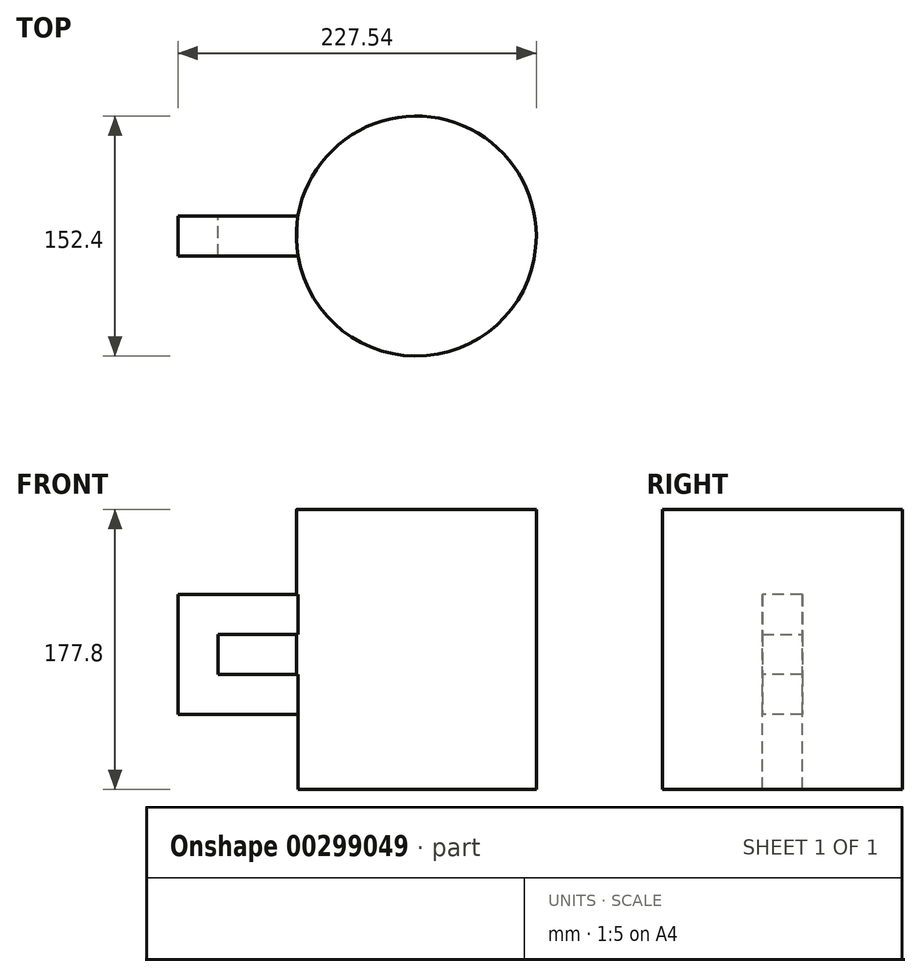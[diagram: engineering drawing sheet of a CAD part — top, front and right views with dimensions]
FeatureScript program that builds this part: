
annotation { "Feature Type Name" : "Feature", "Feature Type Description" : "" }
export const myFeature = defineFeature(function(context is Context, id is Id, definition is map)
    precondition{}
    {
        {
            var Q0;
            Q0=qCreatedBy(makeId("Front.planeOp"),FACE);
            var sketch = newSketch(context, id + "F0", { "sketchPlane" : qUnion([Q0])});
            skLineSegment(sketch, "E0", {"start": v(-88.52, 73.08) * mm, "end": v(-12.32, 73.08) * mm});
            skLineSegment(sketch, "E1", {"start": v(-88.52, 73.08) * mm, "end": v(-88.52, -3.12) * mm});
            skLineSegment(sketch, "E2", {"start": v(-12.32, -3.12) * mm, "end": v(-88.52, -3.12) * mm});
            skLineSegment(sketch, "E3.bottom", {"start": v(-12.32, 47.68) * mm, "end": v(-63.12, 47.68) * mm});
            skLineSegment(sketch, "E3.top", {"start": v(-12.32, 22.28) * mm, "end": v(-63.12, 22.28) * mm});
            skLineSegment(sketch, "E3.right", {"start": v(-63.12, 47.68) * mm, "end": v(-63.12, 22.28) * mm});
            skLineSegment(sketch, "E4", {"start": v(-12.32, 73.08) * mm, "end": v(-12.32, 47.68) * mm});
            skLineSegment(sketch, "E5", {"start": v(-12.32, 22.28) * mm, "end": v(-12.32, -3.12) * mm});
            skSolve(sketch);
        }
        {
            var Q0;
            Q0=makeQuery(id+"F0.imprint","IMPRINT",FACE,{"disambiguationData":[TD([[makeQuery(id+"F0.imprint","IMPRINT",EDGE,{"derivedFrom":sQuery(id+"F0.wireOp",EDGE,"E0")}),-1.0]])]});
            extrude(context, id + "F1", {"entities" : qUnion([Q0]), "depth" : 25.4 * mm, "hasDraft" : true, "draftAngle" : 0 * degree});
        }
        {
            var Q0;
            Q0=qCreatedBy(makeId("Top.planeOp"),FACE);
            var sketch = newSketch(context, id + "F2", { "sketchPlane" : qUnion([Q0])});
            skCircle(sketch, "E6", {"center": v(62.82, -12.7) * mm, "radius": 76.2 * mm});
            skPoint(sketch, "E6.first.point", {"position": v(-12.32, 0) * mm});
            skPoint(sketch, "E6.second.point", {"position": v(-12.32, 0) * mm});
            skPoint(sketch, "E6.third.point", {"position": v(-12.32, -25.4) * mm});
            skSolve(sketch);
        }
        {
            var Q0;
            Q0=makeQuery(id+"F2.imprint","IMPRINT",FACE,{"disambiguationData":[TD([[makeQuery(id+"F2.imprint","IMPRINT",EDGE,{"derivedFrom":sQuery(id+"F2.wireOp",EDGE,"E6")}),1.0]])]});
            extrude(context, id + "F3", {"entities" : qUnion([Q0]), "operationType" : NewBodyOperationType.ADD, "depth" : 127 * mm});
        }
        {
            var Q0;
            Q0=makeQuery(id+"F3.opExtrude","CAP_FACE",FACE,{"disambiguationData":[OSD([sQuery(id+"F2.wireOp",EDGE,"E6")])],"isStart":true});
            extrude(context, id + "F4", {"entities" : qUnion([Q0]), "operationType" : NewBodyOperationType.ADD, "depth" : 50.8 * mm, "hasSecondDirection" : true, "secondDirectionOppositeDirection" : true, "secondDirectionDepth" : 25.4 * mm});
        }
    });
